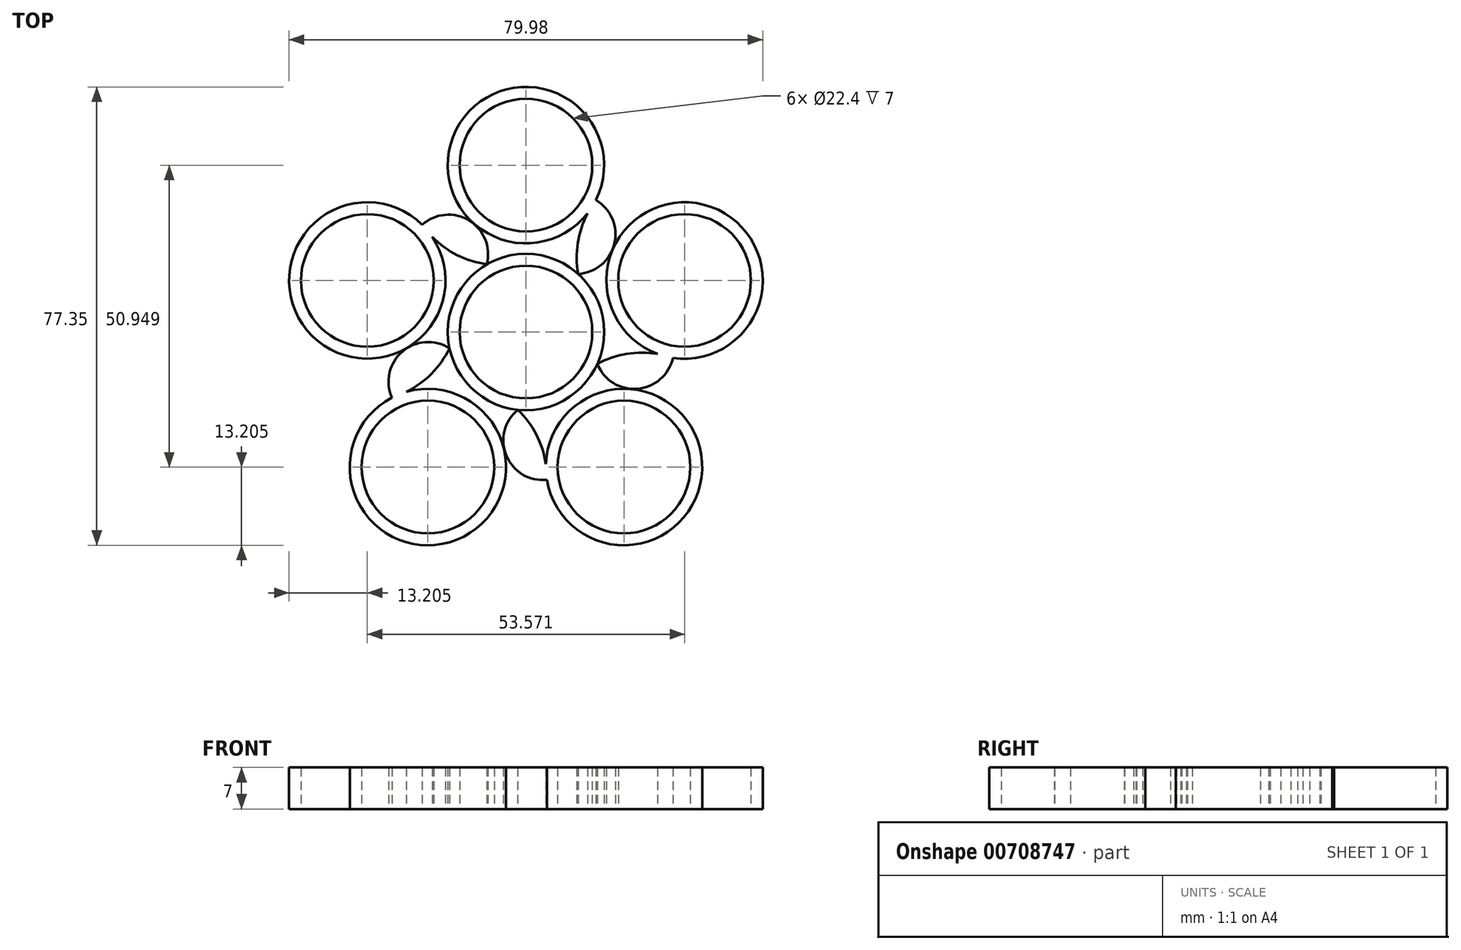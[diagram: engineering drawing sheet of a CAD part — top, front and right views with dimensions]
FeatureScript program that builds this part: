
annotation { "Feature Type Name" : "Feature", "Feature Type Description" : "" }
export const myFeature = defineFeature(function(context is Context, id is Id, definition is map)
    precondition{}
    {
        {
            var Q0;
            Q0=qCreatedBy(makeId("Top.planeOp"),FACE);
            var sketch = newSketch(context, id + "F0", { "sketchPlane" : qUnion([Q0])});
            skCircle(sketch, "E0", {"center": v(0, 0) * mm, "radius": 11.2 * mm});
            skCircle(sketch, "E1", {"center": v(0, 0) * mm, "radius": 13.2 * mm});
            skCircle(sketch, "E2", {"center": v(0, 28.16) * mm, "radius": 11.2 * mm});
            skCircle(sketch, "E3", {"center": v(0, 28.16) * mm, "radius": 13.2 * mm});
            skCircle(sketch, "E4.1.0", {"center": v(-26.79, 8.7) * mm, "radius": 13.2 * mm});
            skCircle(sketch, "E4.1.1", {"center": v(-26.79, 8.7) * mm, "radius": 11.2 * mm});
            skCircle(sketch, "E4.2.0", {"center": v(-16.55, -22.79) * mm, "radius": 13.2 * mm});
            skCircle(sketch, "E4.2.1", {"center": v(-16.55, -22.79) * mm, "radius": 11.2 * mm});
            skCircle(sketch, "E4.3.0", {"center": v(16.55, -22.79) * mm, "radius": 13.2 * mm});
            skCircle(sketch, "E4.3.1", {"center": v(16.55, -22.79) * mm, "radius": 11.2 * mm});
            skCircle(sketch, "E4.4.0", {"center": v(26.79, 8.7) * mm, "radius": 13.2 * mm});
            skCircle(sketch, "E4.4.1", {"center": v(26.79, 8.7) * mm, "radius": 11.2 * mm});
            skArc(sketch, "E5", {"start": v(8.83, 9.81) * mm, "mid": v(14.94, 14.93) * mm, "end": v(11.8, 22.26) * mm});
            skArc(sketch, "E6", {"start": v(11.8, 22.26) * mm, "mid": v(9.01, 16.35) * mm, "end": v(8.83, 9.81) * mm});
            skArc(sketch, "E7.1.0", {"start": v(-6.6, 11.43) * mm, "mid": v(-9.58, 18.82) * mm, "end": v(-17.52, 18.1) * mm});
            skArc(sketch, "E7.1.1", {"start": v(-17.52, 18.1) * mm, "mid": v(-12.76, 13.62) * mm, "end": v(-6.6, 11.43) * mm});
            skArc(sketch, "E7.2.0", {"start": v(-12.91, -2.75) * mm, "mid": v(-20.86, -3.3) * mm, "end": v(-22.64, -11.07) * mm});
            skArc(sketch, "E7.2.1", {"start": v(-22.64, -11.07) * mm, "mid": v(-16.9, -7.93) * mm, "end": v(-12.91, -2.75) * mm});
            skArc(sketch, "E7.3.0", {"start": v(-1.38, -13.13) * mm, "mid": v(-3.31, -20.86) * mm, "end": v(3.53, -24.95) * mm});
            skArc(sketch, "E7.3.1", {"start": v(3.53, -24.95) * mm, "mid": v(2.32, -18.52) * mm, "end": v(-1.38, -13.13) * mm});
            skArc(sketch, "E7.4.0", {"start": v(12.06, -5.37) * mm, "mid": v(18.82, -9.6) * mm, "end": v(24.82, -4.35) * mm});
            skArc(sketch, "E7.4.1", {"start": v(24.82, -4.35) * mm, "mid": v(18.33, -3.52) * mm, "end": v(12.06, -5.37) * mm});
            skSolve(sketch);
        }
        {
            var Q0;
            Q0 = qSketchRegion(id + "F0", true);
            extrude(context, id + "F1", {"entities" : qUnion([Q0]), "depth" : 7 * mm, "offsetDistance" : 25 * mm});
        }
    });
